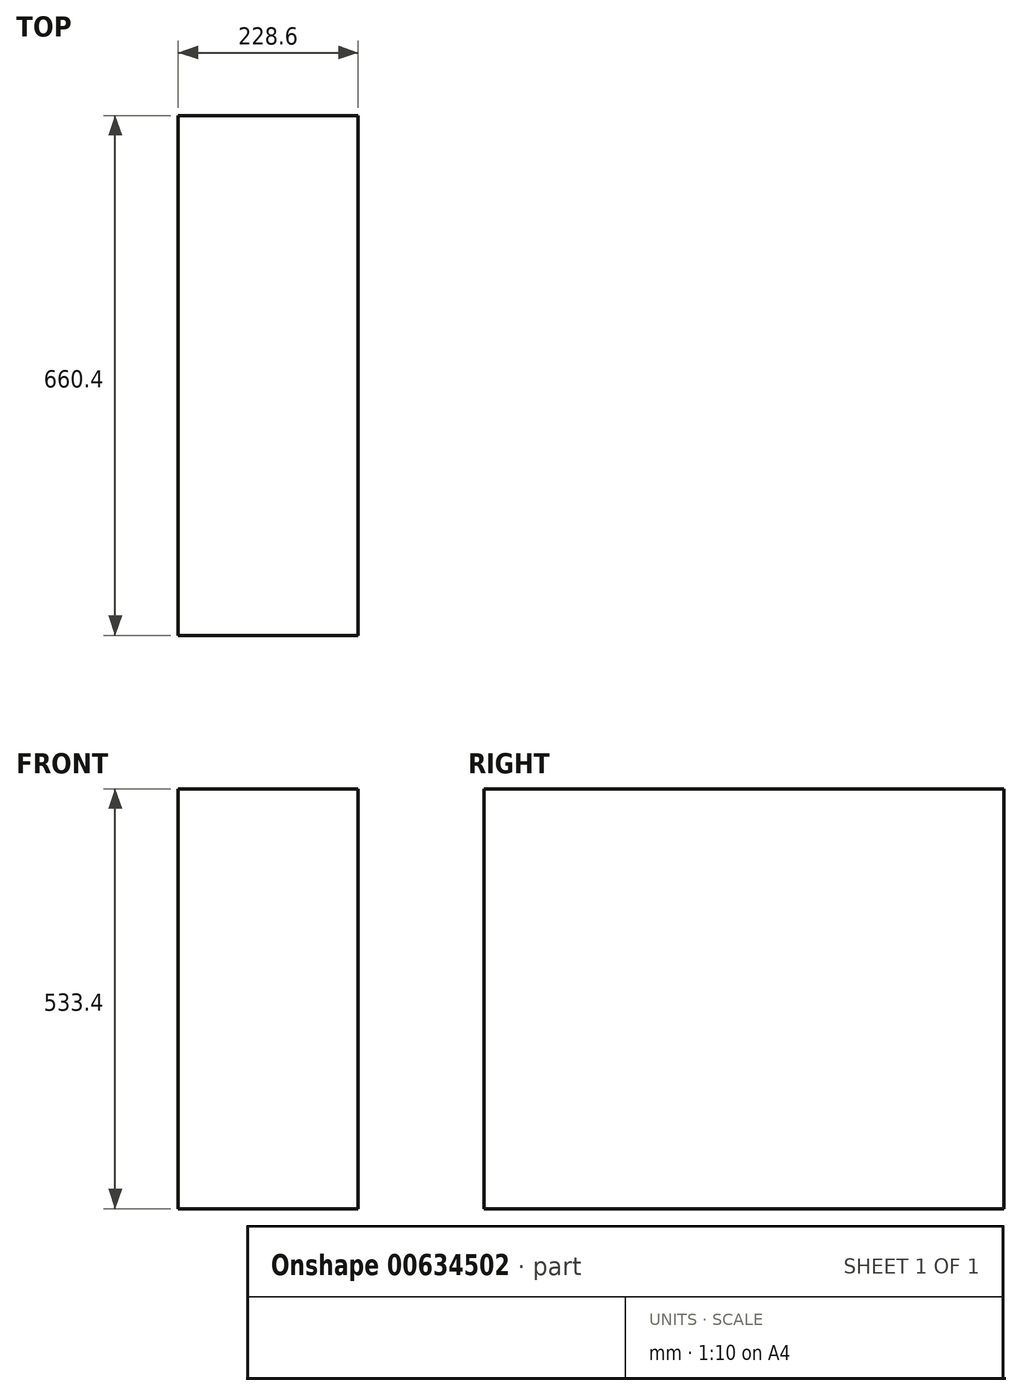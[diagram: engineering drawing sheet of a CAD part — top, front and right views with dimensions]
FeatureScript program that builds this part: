
annotation { "Feature Type Name" : "Feature", "Feature Type Description" : "" }
export const myFeature = defineFeature(function(context is Context, id is Id, definition is map)
    precondition{}
    {
        {
            var Q0;
            Q0=qCreatedBy(makeId("Top.planeOp"),FACE);
            var sketch = newSketch(context, id + "F0", { "sketchPlane" : qUnion([Q0])});
            skLineSegment(sketch, "E0.bottom", {"start": v(0, 0) * mm, "end": v(228.6, 0) * mm});
            skLineSegment(sketch, "E0.top", {"start": v(0, 660.4) * mm, "end": v(228.6, 660.4) * mm});
            skLineSegment(sketch, "E0.left", {"start": v(0, 0) * mm, "end": v(0, 660.4) * mm});
            skLineSegment(sketch, "E0.right", {"start": v(228.6, 0) * mm, "end": v(228.6, 660.4) * mm});
            skSolve(sketch);
        }
        {
            var Q0;
            Q0=makeQuery(id+"F0.imprint","IMPRINT",FACE,{"disambiguationData":[TD([[makeQuery(id+"F0.imprint","IMPRINT",EDGE,{"derivedFrom":sQuery(id+"F0.wireOp",EDGE,"E0.bottom")}),1.0]])]});
            extrude(context, id + "F1", {"entities" : qUnion([Q0]), "depth" : 533.4 * mm});
        }
    });
